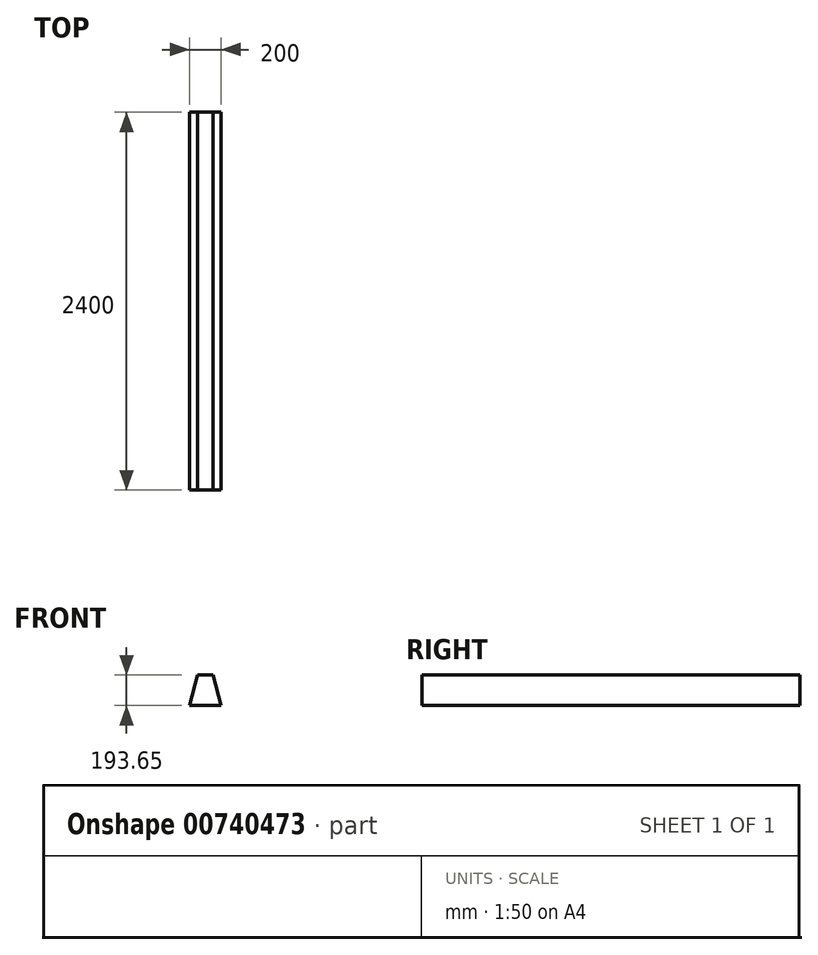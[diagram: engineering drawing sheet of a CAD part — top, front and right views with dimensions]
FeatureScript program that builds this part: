
annotation { "Feature Type Name" : "Feature", "Feature Type Description" : "" }
export const myFeature = defineFeature(function(context is Context, id is Id, definition is map)
    precondition{}
    {
        {
            var Q0;
            Q0=qCreatedBy(makeId("Front.planeOp"),FACE);
            var sketch = newSketch(context, id + "F0", { "sketchPlane" : qUnion([Q0])});
            skLineSegment(sketch, "E0", {"start": v(-100, 0) * mm, "end": v(100, 0) * mm});
            skLineSegment(sketch, "E1", {"start": v(100, 0) * mm, "end": v(50, 193.65) * mm});
            skLineSegment(sketch, "E2", {"start": v(50, 193.65) * mm, "end": v(-50, 193.65) * mm});
            skLineSegment(sketch, "E3", {"start": v(-50, 193.65) * mm, "end": v(-100, 0) * mm});
            skSolve(sketch);
        }
        {
            var Q0;
            Q0=qCreatedBy(makeId("Top.planeOp"),FACE);
            var sketch = newSketch(context, id + "F1", { "sketchPlane" : qUnion([Q0])});
            skLineSegment(sketch, "E4", {"start": v(0, 0) * mm, "end": v(0, 2400) * mm});
            skSolve(sketch);
        }
        {
            var Q0;
            Q0 = qSketchRegion(id + "F0", true);
            var Q1;
            Q1 = qConstructionFilter(qBodyType(qCreatedBy(id + "F1" ,EDGE), BodyType.WIRE), ConstructionObject.NO);
            sweep(context, id + "F2", {"profiles" : qUnion([Q0]), "path" : qUnion([Q1])});
        }
    });
